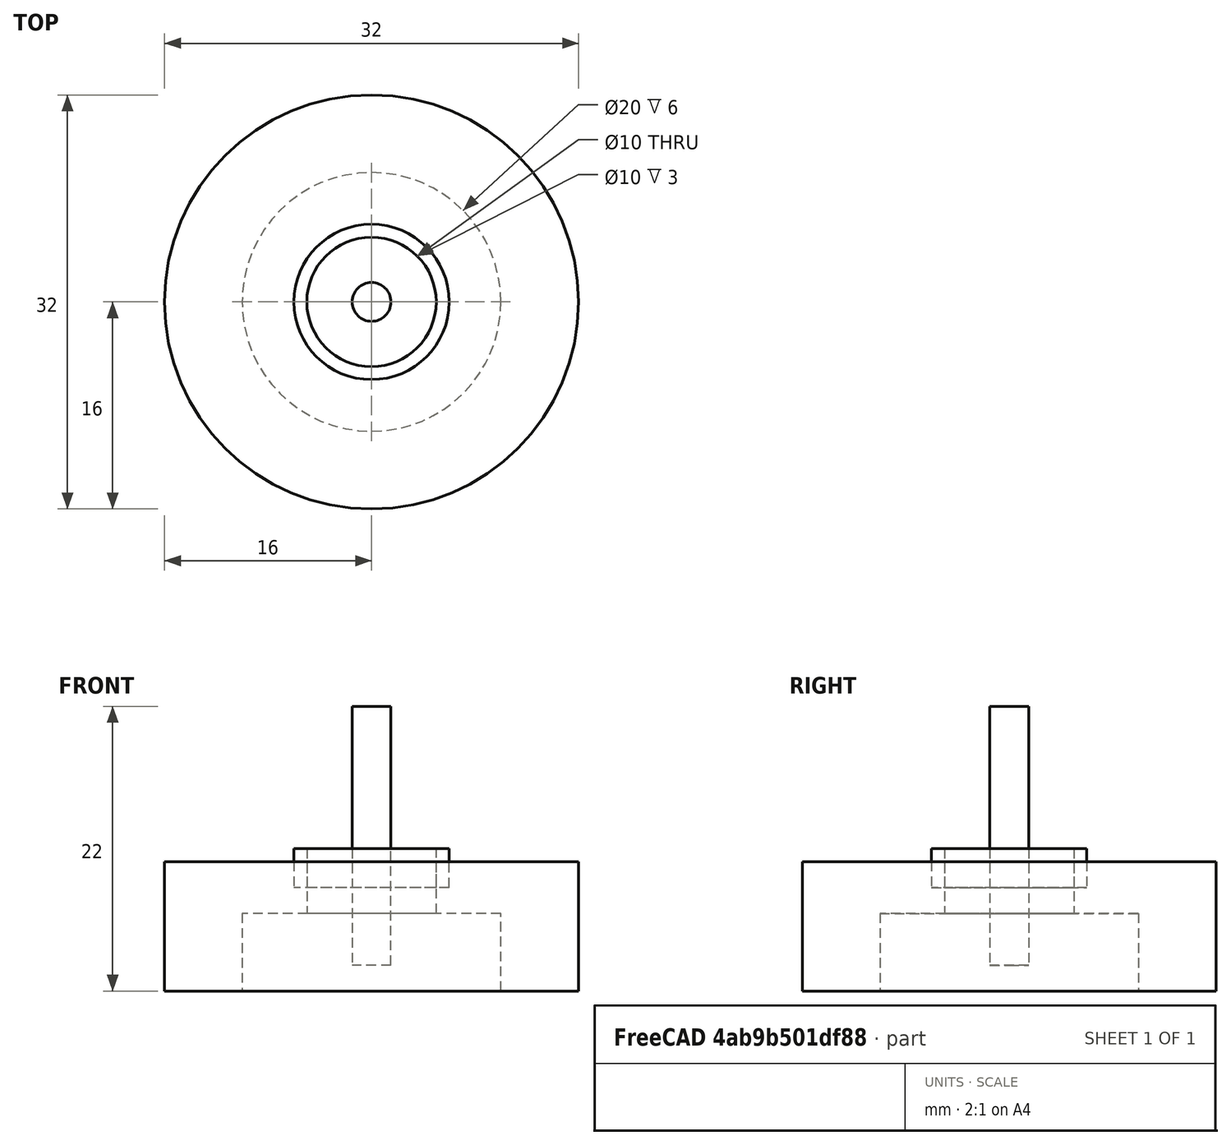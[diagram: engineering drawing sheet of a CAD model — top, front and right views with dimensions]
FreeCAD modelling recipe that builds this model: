
FCSTD DOCUMENT  (FreeCAD 1.0R39285 (Git))
Label: micromouse_wheels
License: All rights reserved
LicenseURL: https://en.wikipedia.org/wiki/All_rights_reserved
objects: Part::Cylinder×6, Part::Cut×3, PartDesign::Body×1, App::Part×1
note: 10 computed .brp shape members not serialized (recipe doc carries the construction recipe); baked Part::Feature solids carry a one-line shape summary decoded from their .brp

FEATURE [PartDesign::Body] Body
  AllowCompound = false
  Origin = -> Origin001
FEATURE [Part::Cylinder] Cylinder
  Angle = 360
  AttacherType = Attacher::AttachEngine3D
  FirstAngle = 0
  Height = 10
  Radius = 16
  SecondAngle = 0
FEATURE [Part::Cylinder] Cylinder001
  Angle = 360
  AttacherType = Attacher::AttachEngine3D
  FirstAngle = 0
  Height = 6
  Radius = 10
  SecondAngle = 0
FEATURE [Part::Cut] Cut
  Base = -> Cylinder
  Tool = -> Cylinder001
FEATURE [Part::Cylinder] Cylinder002
  Angle = 360
  AttacherType = Attacher::AttachEngine3D
  FirstAngle = 0
  Height = 12
  Radius = 5
  SecondAngle = 0
FEATURE [Part::Cut] Cut001
  Base = -> Cut
  Tool = -> Cylinder002
FEATURE [Part::Cylinder] Cylinder005
  Angle = 360
  AttacherType = Attacher::AttachEngine3D
  FirstAngle = 0
  Height = 20
  Placement = pos=(0,0,2) rot=(0,0,1;0rad)
  Radius = 1.5
  SecondAngle = 0
FEATURE [Part::Cylinder] Cylinder003
  Angle = 360
  AttacherType = Attacher::AttachEngine3D
  FirstAngle = 0
  Height = 3
  Placement = pos=(0,0,8) rot=(0,0,1;0rad)
  Radius = 6
  SecondAngle = 0
FEATURE [Part::Cylinder] Cylinder004
  Angle = 360
  AttacherType = Attacher::AttachEngine3D
  FirstAngle = 0
  Height = 13
  Radius = 5
  SecondAngle = 0
FEATURE [Part::Cut] Cut002
  Base = -> Cylinder003
  Tool = -> Cylinder004
FEATURE [App::Part] Part  label="wheel30mm"
  Group = -> [Body,Cylinder002,Cylinder,Cut,Cylinder001,Cut001,Cylinder004,Cylinder003,Cut002,Cylinder005]
  Origin = -> Origin
